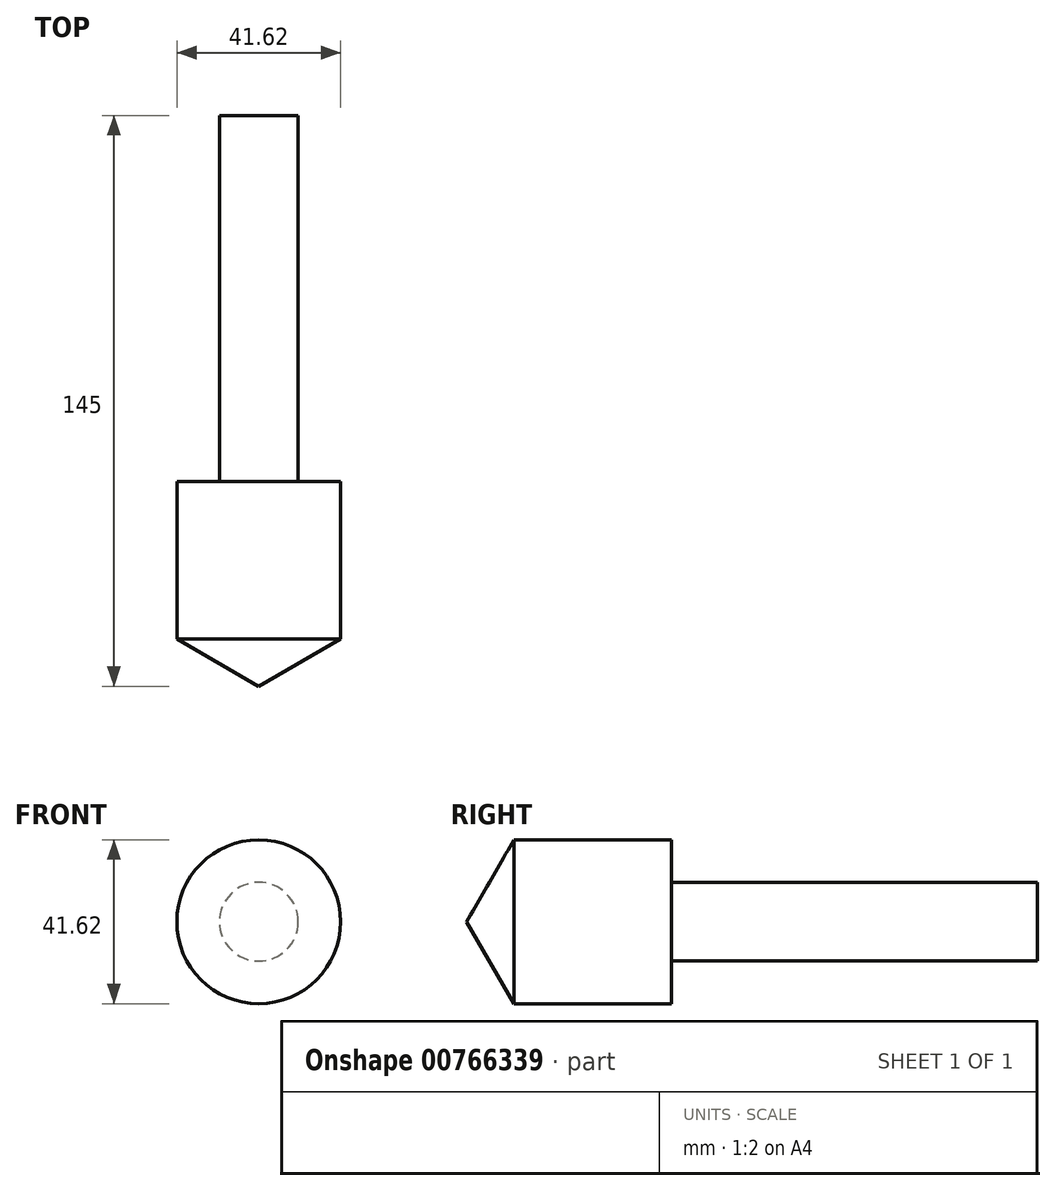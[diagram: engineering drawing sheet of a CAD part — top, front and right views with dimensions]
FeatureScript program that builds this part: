
annotation { "Feature Type Name" : "Feature", "Feature Type Description" : "" }
export const myFeature = defineFeature(function(context is Context, id is Id, definition is map)
    precondition{}
    {
        {
            var Q0;
            Q0=qCreatedBy(makeId("Top.planeOp"),FACE);
            var sketch = newSketch(context, id + "F0", { "sketchPlane" : qUnion([Q0])});
            skLineSegment(sketch, "E0", {"start": v(-10, 76.07) * mm, "end": v(0, 76.07) * mm});
            skLineSegment(sketch, "E1", {"start": v(-10, 76.07) * mm, "end": v(-10, -16.91) * mm});
            skLineSegment(sketch, "E2", {"start": v(-10, -16.91) * mm, "end": v(-20.81, -16.91) * mm});
            skLineSegment(sketch, "E3", {"start": v(-20.81, -16.91) * mm, "end": v(-20.81, -56.91) * mm});
            skLineSegment(sketch, "E4", {"start": v(-20.81, -56.91) * mm, "end": v(0, -56.91) * mm});
            skLineSegment(sketch, "E5", {"start": v(0, 76.07) * mm, "end": v(0, -68.93) * mm});
            skLineSegment(sketch, "E6", {"start": v(-20.81, -56.91) * mm, "end": v(0, -68.93) * mm});
            skSolve(sketch);
        }
        {
            var Q0;
            Q0 = qSketchRegion(id + "F0", true);
            var Q1;
            Q1=sQuery(id+"F0.wireOp",EDGE,"E5");
            revolve(context, id + "F1", {"surfaceOperationType" : NewSurfaceOperationType.NEW, "entities" : qUnion([Q0]), "axis" : qUnion([Q1]), "revolveType" : RevolveType.FULL});
        }
    });
